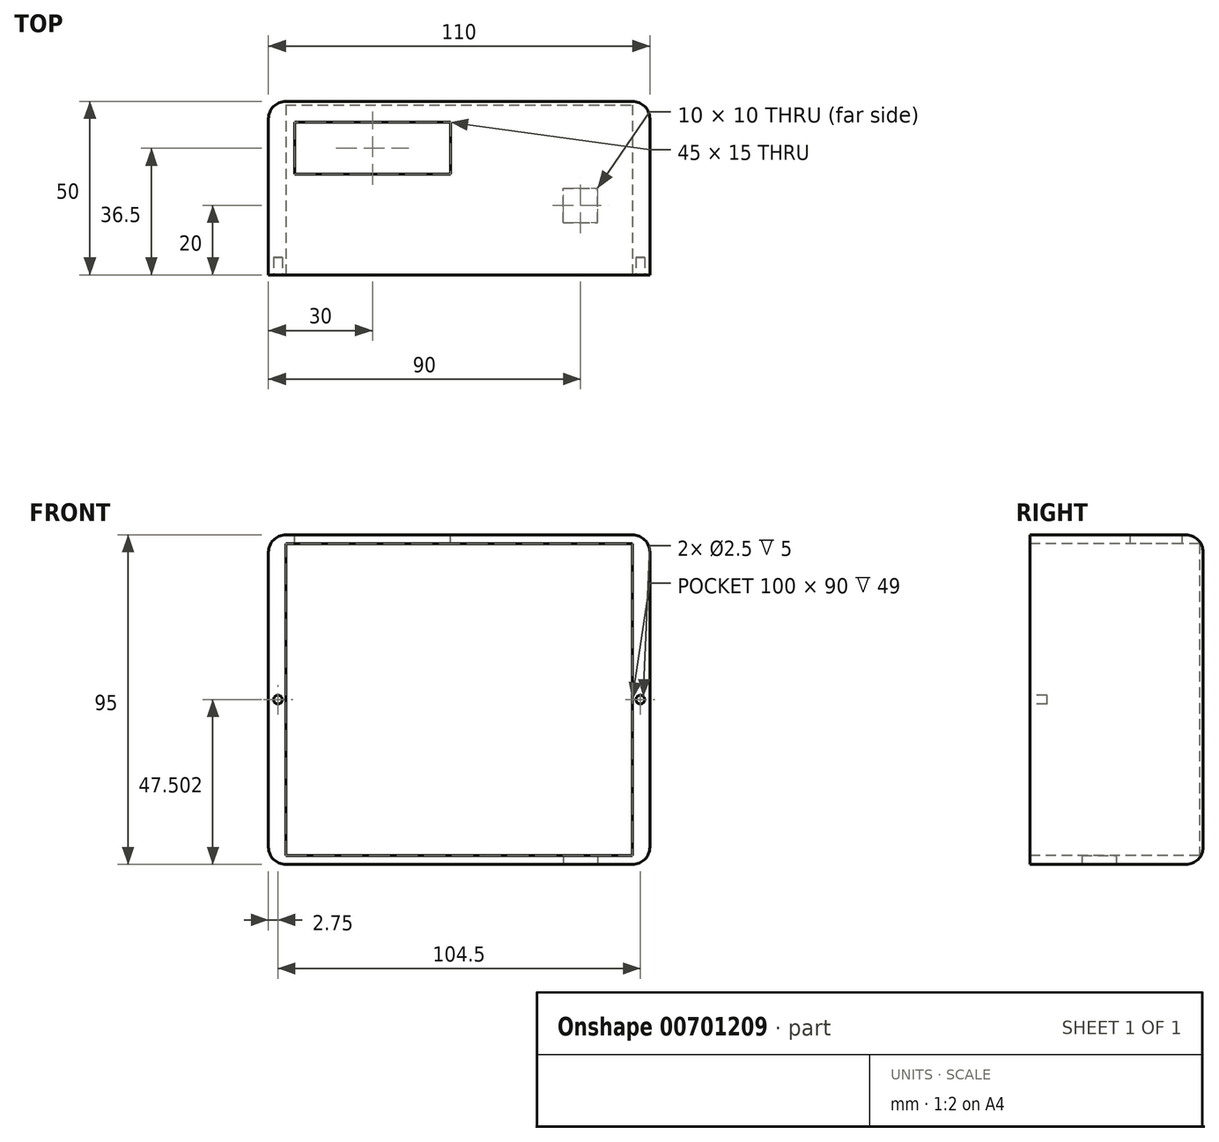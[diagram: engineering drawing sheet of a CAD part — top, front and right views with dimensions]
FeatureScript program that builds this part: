
annotation { "Feature Type Name" : "Feature", "Feature Type Description" : "" }
export const myFeature = defineFeature(function(context is Context, id is Id, definition is map)
    precondition{}
    {
        {
            var Q0;
            Q0=qCreatedBy(makeId("Front.planeOp"),FACE);
            var sketch = newSketch(context, id + "F0", { "sketchPlane" : qUnion([Q0])});
            skLineSegment(sketch, "E0.bottom", {"start": v(-72.19, 25.34) * mm, "end": v(37.81, 25.34) * mm});
            skLineSegment(sketch, "E0.top", {"start": v(-72.19, -69.66) * mm, "end": v(37.81, -69.66) * mm});
            skLineSegment(sketch, "E0.left", {"start": v(-72.19, 25.34) * mm, "end": v(-72.19, -69.66) * mm});
            skLineSegment(sketch, "E0.right", {"start": v(37.81, 25.34) * mm, "end": v(37.81, -69.66) * mm});
            skSolve(sketch);
        }
        {
            var Q0;
            Q0 = qSketchRegion(id + "F0", true);
            extrude(context, id + "F1", {"entities" : qUnion([Q0]), "depth" : 50 * mm, "offsetDistance" : 25 * mm});
        }
        {
            var Q0;
            Q0=makeQuery(id+"F1.opExtrude","CAP_FACE",FACE,{"disambiguationData":[OSD([sQuery(id+"F0.wireOp",EDGE,"E0.bottom"),sQuery(id+"F0.wireOp",EDGE,"E0.top"),sQuery(id+"F0.wireOp",EDGE,"E0.left"),sQuery(id+"F0.wireOp",EDGE,"E0.right")])],"isStart":false});
            var sketch = newSketch(context, id + "F2", { "sketchPlane" : qUnion([Q0])});
            skLineSegment(sketch, "E1.bottom", {"start": v(-67.19, 22.84) * mm, "end": v(32.81, 22.84) * mm});
            skLineSegment(sketch, "E1.top", {"start": v(-67.19, -67.16) * mm, "end": v(32.81, -67.16) * mm});
            skLineSegment(sketch, "E1.left", {"start": v(-67.19, 22.84) * mm, "end": v(-67.19, -67.16) * mm});
            skLineSegment(sketch, "E1.right", {"start": v(32.81, 22.84) * mm, "end": v(32.81, -67.16) * mm});
            skSolve(sketch);
        }
        {
            var Q0;
            Q0 = qSketchRegion(id + "F2", true);
            extrude(context, id + "F3", {"entities" : qUnion([Q0]), "operationType" : NewBodyOperationType.REMOVE, "oppositeDirection" : true, "depth" : 49 * mm, "offsetDistance" : 25 * mm});
        }
        {
            var Q0;
            Q0=makeQuery(id+"F1.opExtrude","CAP_FACE",FACE,{"disambiguationData":[OSD([sQuery(id+"F0.wireOp",EDGE,"E0.bottom"),sQuery(id+"F0.wireOp",EDGE,"E0.top"),sQuery(id+"F0.wireOp",EDGE,"E0.left"),sQuery(id+"F0.wireOp",EDGE,"E0.right")])],"isStart":false});
            var sketch = newSketch(context, id + "F4", { "sketchPlane" : qUnion([Q0])});
            skCircle(sketch, "E2", {"center": v(-69.44, -22.16) * mm, "radius": 1.25 * mm});
            skCircle(sketch, "E3", {"center": v(35.06, -22.16) * mm, "radius": 1.25 * mm});
            skSolve(sketch);
        }
        {
            var Q0;
            Q0 = qSketchRegion(id + "F4", true);
            extrude(context, id + "F5", {"entities" : qUnion([Q0]), "operationType" : NewBodyOperationType.REMOVE, "oppositeDirection" : true, "depth" : 5 * mm, "offsetDistance" : 25 * mm});
        }
        {
            var Q0;
            Q0=makeQuery(id+"F1.opExtrude","SWEPT_EDGE",EDGE,{"disambiguationData":[OSD([sQuery(id+"F0.wireOp",EDGE,"E0.top"),sQuery(id+"F0.wireOp",EDGE,"E0.left")])]});
            var Q1;
            Q1=makeQuery(id+"F1.opExtrude","SWEPT_EDGE",EDGE,{"disambiguationData":[OSD([sQuery(id+"F0.wireOp",EDGE,"E0.bottom"),sQuery(id+"F0.wireOp",EDGE,"E0.left")])]});
            var Q2;
            Q2=makeQuery(id+"F1.opExtrude","SWEPT_EDGE",EDGE,{"disambiguationData":[OSD([sQuery(id+"F0.wireOp",EDGE,"E0.top"),sQuery(id+"F0.wireOp",EDGE,"E0.right")])]});
            var Q3;
            Q3=makeQuery(id+"F1.opExtrude","SWEPT_EDGE",EDGE,{"disambiguationData":[OSD([sQuery(id+"F0.wireOp",EDGE,"E0.bottom"),sQuery(id+"F0.wireOp",EDGE,"E0.right")])]});
            var Q4;
            Q4=makeQuery(id+"F1.opExtrude","CAP_EDGE",EDGE,{"disambiguationData":[OSD([sQuery(id+"F0.wireOp",EDGE,"E0.right")])],"isStart":true});
            var Q5;
            Q5=makeQuery(id+"F1.opExtrude","CAP_EDGE",EDGE,{"disambiguationData":[OSD([sQuery(id+"F0.wireOp",EDGE,"E0.left")])],"isStart":true});
            var Q6;
            Q6=makeQuery(id+"F1.opExtrude","CAP_EDGE",EDGE,{"disambiguationData":[OSD([sQuery(id+"F0.wireOp",EDGE,"E0.top")])],"isStart":true});
            var Q7;
            Q7=makeQuery(id+"F1.opExtrude","CAP_EDGE",EDGE,{"disambiguationData":[OSD([sQuery(id+"F0.wireOp",EDGE,"E0.bottom")])],"isStart":true});
            fillet(context, id + "F6", {"entities" : qUnion([Q0, Q1, Q2, Q3, Q4, Q5, Q6, Q7]), "radius" : 5 * mm, "tangentPropagation" : true, "allowEdgeOverflow" : false});
        }
        {
            var Q0;
            Q0=makeQuery(id+"F1.opExtrude","SWEPT_FACE",FACE,{"disambiguationData":[OSD([sQuery(id+"F0.wireOp",EDGE,"E0.bottom")])]});
            var sketch = newSketch(context, id + "F7", { "sketchPlane" : qUnion([Q0])});
            skLineSegment(sketch, "E4.bottom", {"start": v(-19.69, -21) * mm, "end": v(-64.69, -21) * mm});
            skLineSegment(sketch, "E4.top", {"start": v(-19.69, -6) * mm, "end": v(-64.69, -6) * mm});
            skLineSegment(sketch, "E4.left", {"start": v(-19.69, -21) * mm, "end": v(-19.69, -6) * mm});
            skLineSegment(sketch, "E4.right", {"start": v(-64.69, -21) * mm, "end": v(-64.69, -6) * mm});
            skSolve(sketch);
        }
        {
            var Q0;
            Q0 = qSketchRegion(id + "F7", true);
            extrude(context, id + "F8", {"entities" : qUnion([Q0]), "operationType" : NewBodyOperationType.REMOVE, "oppositeDirection" : true, "depth" : 25 * mm, "offsetDistance" : 25 * mm});
        }
        {
            var Q0;
            Q0=makeQuery(id+"F1.opExtrude","SWEPT_FACE",FACE,{"disambiguationData":[OSD([sQuery(id+"F0.wireOp",EDGE,"E0.top")])]});
            var sketch = newSketch(context, id + "F9", { "sketchPlane" : qUnion([Q0])});
            skLineSegment(sketch, "E5.bottom", {"start": v(12.81, 35) * mm, "end": v(22.81, 35) * mm});
            skLineSegment(sketch, "E5.top", {"start": v(12.81, 25) * mm, "end": v(22.81, 25) * mm});
            skLineSegment(sketch, "E5.left", {"start": v(12.81, 35) * mm, "end": v(12.81, 25) * mm});
            skLineSegment(sketch, "E5.right", {"start": v(22.81, 35) * mm, "end": v(22.81, 25) * mm});
            skSolve(sketch);
        }
        {
            var Q0;
            Q0 = qSketchRegion(id + "F9", true);
            extrude(context, id + "F10", {"entities" : qUnion([Q0]), "operationType" : NewBodyOperationType.REMOVE, "oppositeDirection" : true, "depth" : 5 * mm, "offsetDistance" : 25 * mm});
        }
    });
